# Revit family: 305_2fcc36913fff42658b252661b703e2
name_source: partatom
category: Pipe Accessories
units: mm (PartAtom-declared; Revit-internal decimal feet)

## family parameters
Always vertical = Yes
Cut with Voids When Loaded = No
Part Type = Valve - Breaks Into
Round Connector Dimension = Use Diameter
Shared = No
Work Plane-Based = No

## types (11) — shared parameters
CAT0 = Yes
CAT0G = No
CATG = No
CATL = No
Description = Cast iron butterfly PN16/PN10, NBR seat, S.S. disc
GH2 = 2 mm  [stored 0.00656168 ft]
GH4 = 4 mm  [stored 0.0131234 ft]
GH4__ve = -4 mm  [stored -0.0131234 ft]
GR3 = 2 mm  [stored 0.00656168 ft]
L2D = 52 mm
L2D_Min = 3048 mm
Manufacturer = VIR
QmdConnectorList = 301;D;302;D
URL = http://www.vironline.com
VERG = No
VERL = Yes
W2D = 100 mm
magiPartTypeId = 305
magiProductFamilyId = 2fcc36913fff42658b252661b703e2

## per-type parameters (varying)
- 4029L DN100: D=100 mm; GB=53 mm; GH3=236 mm; GL1=153 mm; GL2=149 mm; GL3=10 mm  [stored 0.0328084 ft]; GR1=73 mm; H5=137 mm; H5__ve=-137 mm; HA=114 mm; HB=200 mm; L=52 mm; L1=6 mm  [stored 0.019685 ft]; L2=41 mm; LH1=232 mm; LH2=32 mm; LH2__ve=-32 mm  [stored -0.104987 ft]; LH3=32 mm; LH3__ve=-32 mm  [stored -0.104987 ft]; LL=267 mm; L_2=26 mm; R=50 mm; R1=63 mm; R2=77 mm; R4=45 mm; R5=6 mm  [stored 0.019685 ft]; S=13 mm  [stored 0.0426509 ft]; S__ve=-13 mm  [stored -0.0426509 ft]; W1=6 mm  [stored 0.019685 ft]; W1__ve=-6 mm; W5=14 mm  [stored 0.0459318 ft]; magiProductId=dbbac9561acd4e72b5f56e0b8b419c
- 4029L DN125: D=125 mm; GB=53 mm; GH3=249 mm; GL1=153 mm; GL2=149 mm; GL3=10 mm  [stored 0.0328084 ft]; GR1=73 mm; H5=136 mm; H5__ve=-136 mm; HA=127 mm; HB=213 mm; L=56 mm; L1=6 mm  [stored 0.019685 ft]; L2=44 mm; LH1=245 mm; LH2=32 mm; LH2__ve=-32 mm  [stored -0.104987 ft]; LH3=32 mm; LH3__ve=-32 mm  [stored -0.104987 ft]; LL=267 mm; L_2=28 mm; R=63 mm; R1=77 mm; R2=91 mm; R4=45 mm; R5=7 mm  [stored 0.0229659 ft]; S=13 mm  [stored 0.0426509 ft]; S__ve=-13 mm  [stored -0.0426509 ft]; W1=7 mm  [stored 0.0229659 ft]; W1__ve=-7 mm  [stored -0.0229659 ft]; W5=15 mm  [stored 0.0492126 ft]; magiProductId=3ed8022d35d848de8aed421a92bef1
- 4029L DN150: D=150 mm; GB=53 mm; GH3=261 mm; GL1=153 mm; GL2=149 mm; GL3=10 mm  [stored 0.0328084 ft]; GR1=73 mm; H5=135 mm; H5__ve=-135 mm  [stored -0.442913 ft]; HA=140 mm; HB=225 mm; L=56 mm; L1=6 mm  [stored 0.019685 ft]; L2=44 mm; LH1=257 mm; LH2=32 mm; LH2__ve=-32 mm  [stored -0.104987 ft]; LH3=32 mm; LH3__ve=-32 mm  [stored -0.104987 ft]; LL=267 mm; L_2=28 mm; R=75 mm; R1=90 mm; R2=105 mm; R4=45 mm; R5=7 mm  [stored 0.0229659 ft]; S=13 mm  [stored 0.0426509 ft]; S__ve=-13 mm  [stored -0.0426509 ft]; W1=7 mm  [stored 0.0229659 ft]; W1__ve=-7 mm  [stored -0.0229659 ft]; W5=15 mm  [stored 0.0492126 ft]; magiProductId=f218716140be4eb1a59fd1333bbf94
- 4029L DN200: D=200 mm; GB=73 mm; GH3=298 mm; GL1=236 mm; GL2=232 mm; GL3=35 mm; GR1=145 mm; H5=144 mm; H5__ve=-144 mm; HA=173 mm; HB=260 mm; L=60 mm; L1=7 mm  [stored 0.0229659 ft]; L2=47 mm; LH1=296 mm; LH2=36 mm; LH2__ve=-36 mm  [stored -0.11811 ft]; LH3=36 mm; LH3__ve=-36 mm  [stored -0.11811 ft]; LL=359 mm; L_2=30 mm; R=100 mm; R1=116 mm; R2=132 mm; R4=63 mm; R5=9 mm  [stored 0.0295276 ft]; S=14 mm  [stored 0.0459318 ft]; S__ve=-14 mm  [stored -0.0459318 ft]; W1=9 mm  [stored 0.0295276 ft]; W1__ve=-9 mm; W5=16 mm  [stored 0.0524934 ft]; magiProductId=3e85225e54db4ae986d0009b540353
- 4029L DN250: D=250 mm; GB=73 mm; GH3=330 mm; GL1=236 mm; GL2=232 mm; GL3=35 mm; GR1=145 mm; H5=150 mm; H5__ve=-150 mm  [stored -0.492126 ft]; HA=203 mm; HB=292 mm; L=68 mm; L1=7 mm  [stored 0.0229659 ft]; L2=53 mm; LH1=328 mm; LH2=36 mm; LH2__ve=-36 mm  [stored -0.11811 ft]; LH3=36 mm; LH3__ve=-36 mm  [stored -0.11811 ft]; LL=359 mm; L_2=34 mm; R=125 mm; R1=143 mm; R2=160 mm; R4=63 mm; R5=11 mm  [stored 0.0360892 ft]; S=14 mm  [stored 0.0459318 ft]; S__ve=-14 mm  [stored -0.0459318 ft]; W1=11 mm  [stored 0.0360892 ft]; W1__ve=-11 mm  [stored -0.0360892 ft]; W5=18 mm  [stored 0.0590551 ft]; magiProductId=744ed571e4124a688bf0438e2e6ce2
- 4029L DN300: D=300 mm; GB=80 mm; GH3=377 mm; GL1=231 mm; GL2=227 mm; GL3=39 mm; GR1=145 mm; H5=169 mm; H5__ve=-169 mm; HA=242 mm; HB=337 mm; L=78 mm; L1=9 mm  [stored 0.0295276 ft]; L2=61 mm; LH1=373 mm; LH2=36 mm; LH2__ve=-36 mm  [stored -0.11811 ft]; LH3=36 mm; LH3__ve=-36 mm  [stored -0.11811 ft]; LL=359 mm; L_2=39 mm; R=150 mm; R1=168 mm; R2=187 mm; R4=75 mm; R5=11 mm  [stored 0.0360892 ft]; S=20 mm  [stored 0.0656168 ft]; S__ve=-20 mm  [stored -0.0656168 ft]; W1=11 mm  [stored 0.0360892 ft]; W1__ve=-11 mm  [stored -0.0360892 ft]; W5=20 mm  [stored 0.0656168 ft]; magiProductId=5ccd9642bbdb4f74bf6c2781b39a49
- 4029L DN32: D=32 mm; GB=53 mm; GH3=156 mm; GL1=153 mm; GL2=149 mm; GL3=10 mm  [stored 0.0328084 ft]; GR1=73 mm; H5=93 mm; H5__ve=-93 mm; HA=65 mm; HB=120 mm; L=33 mm; L1=4 mm  [stored 0.0131234 ft]; L2=26 mm; LH1=152 mm; LH2=32 mm; LH2__ve=-32 mm  [stored -0.104987 ft]; LH3=32 mm; LH3__ve=-32 mm  [stored -0.104987 ft]; LL=267 mm; L_2=17 mm  [stored 0.0557743 ft]; R=16 mm  [stored 0.0524934 ft]; R1=27 mm; R2=39 mm; R4=45 mm; R5=3 mm  [stored 0.00984252 ft]; S=11 mm  [stored 0.0360892 ft]; S__ve=-11 mm  [stored -0.0360892 ft]; W1=3 mm  [stored 0.00984252 ft]; W1__ve=-3 mm  [stored -0.00984252 ft]; W5=9 mm  [stored 0.0295276 ft]; magiProductId=f8d87f180c264a789c2892ecff03f5
- 4029L DN40: D=40 mm; GB=53 mm; GH3=156 mm; GL1=153 mm; GL2=149 mm; GL3=10 mm  [stored 0.0328084 ft]; GR1=73 mm; H5=88 mm; H5__ve=-88 mm; HA=75 mm; HB=120 mm; L=33 mm; L1=4 mm  [stored 0.0131234 ft]; L2=26 mm; LH1=152 mm; LH2=32 mm; LH2__ve=-32 mm  [stored -0.104987 ft]; LH3=32 mm; LH3__ve=-32 mm  [stored -0.104987 ft]; LL=267 mm; L_2=17 mm  [stored 0.0557743 ft]; R=20 mm  [stored 0.0656168 ft]; R1=32 mm; R2=43 mm; R4=45 mm; R5=3 mm  [stored 0.00984252 ft]; S=11 mm  [stored 0.0360892 ft]; S__ve=-11 mm  [stored -0.0360892 ft]; W1=3 mm  [stored 0.00984252 ft]; W1__ve=-3 mm  [stored -0.00984252 ft]; W5=9 mm  [stored 0.0295276 ft]; magiProductId=22229942cfd2483ab5e95423a88c47
- 4029L DN50: D=50 mm; GB=53 mm; GH3=198 mm; GL1=153 mm; GL2=149 mm; GL3=10 mm  [stored 0.0328084 ft]; GR1=73 mm; H5=125 mm; H5__ve=-125 mm  [stored -0.410105 ft]; HA=76 mm; HB=162 mm; L=43 mm; L1=5 mm  [stored 0.0164042 ft]; L2=34 mm; LH1=194 mm; LH2=32 mm; LH2__ve=-32 mm  [stored -0.104987 ft]; LH3=32 mm; LH3__ve=-32 mm  [stored -0.104987 ft]; LL=267 mm; L_2=22 mm; R=25 mm; R1=38 mm; R2=50 mm; R4=45 mm; R5=4 mm  [stored 0.0131234 ft]; S=13 mm  [stored 0.0426509 ft]; S__ve=-13 mm  [stored -0.0426509 ft]; W1=4 mm  [stored 0.0131234 ft]; W1__ve=-4 mm  [stored -0.0131234 ft]; W5=11 mm  [stored 0.0360892 ft]; magiProductId=b0012455985d4d5ca6de00f1b5eacd
- 4029L DN65: D=65 mm; GB=53 mm; GH3=211 mm; GL1=153 mm; GL2=149 mm; GL3=10 mm  [stored 0.0328084 ft]; GR1=73 mm; H5=129 mm; H5__ve=-129 mm; HA=89 mm; HB=175 mm; L=46 mm; L1=5 mm  [stored 0.0164042 ft]; L2=36 mm; LH1=207 mm; LH2=32 mm; LH2__ve=-32 mm  [stored -0.104987 ft]; LH3=32 mm; LH3__ve=-32 mm  [stored -0.104987 ft]; LL=267 mm; L_2=23 mm; R=33 mm; R1=46 mm; R2=59 mm; R4=45 mm; R5=4 mm  [stored 0.0131234 ft]; S=13 mm  [stored 0.0426509 ft]; S__ve=-13 mm  [stored -0.0426509 ft]; W1=4 mm  [stored 0.0131234 ft]; W1__ve=-4 mm  [stored -0.0131234 ft]; W5=12 mm  [stored 0.0393701 ft]; magiProductId=80aa370edbf94f0ab04f6b32d9d907
- 4029L DN80: D=80 mm; GB=53 mm; GH3=217 mm; GL1=153 mm; GL2=149 mm; GL3=10 mm  [stored 0.0328084 ft]; GR1=73 mm; H5=128 mm; H5__ve=-128 mm; HA=95 mm; HB=181 mm; L=46 mm; L1=5 mm  [stored 0.0164042 ft]; L2=36 mm; LH1=213 mm; LH2=32 mm; LH2__ve=-32 mm  [stored -0.104987 ft]; LH3=32 mm; LH3__ve=-32 mm  [stored -0.104987 ft]; LL=267 mm; L_2=23 mm; R=40 mm; R1=53 mm; R2=67 mm; R4=45 mm; R5=5 mm  [stored 0.0164042 ft]; S=13 mm  [stored 0.0426509 ft]; S__ve=-13 mm  [stored -0.0426509 ft]; W1=5 mm  [stored 0.0164042 ft]; W1__ve=-5 mm  [stored -0.0164042 ft]; W5=12 mm  [stored 0.0393701 ft]; magiProductId=178dc604cf084b2ba51efd9b5b01bd

note: column(s) folded — value = type name in every type: MC Product Code

note: [stored X ft] marks values corroborated as IEEE doubles in the binary element streams (Revit-internal decimal feet)

## geometry (parser evidence)
native form markers: Sweep x1
no freeform markers — native parametric forms only
